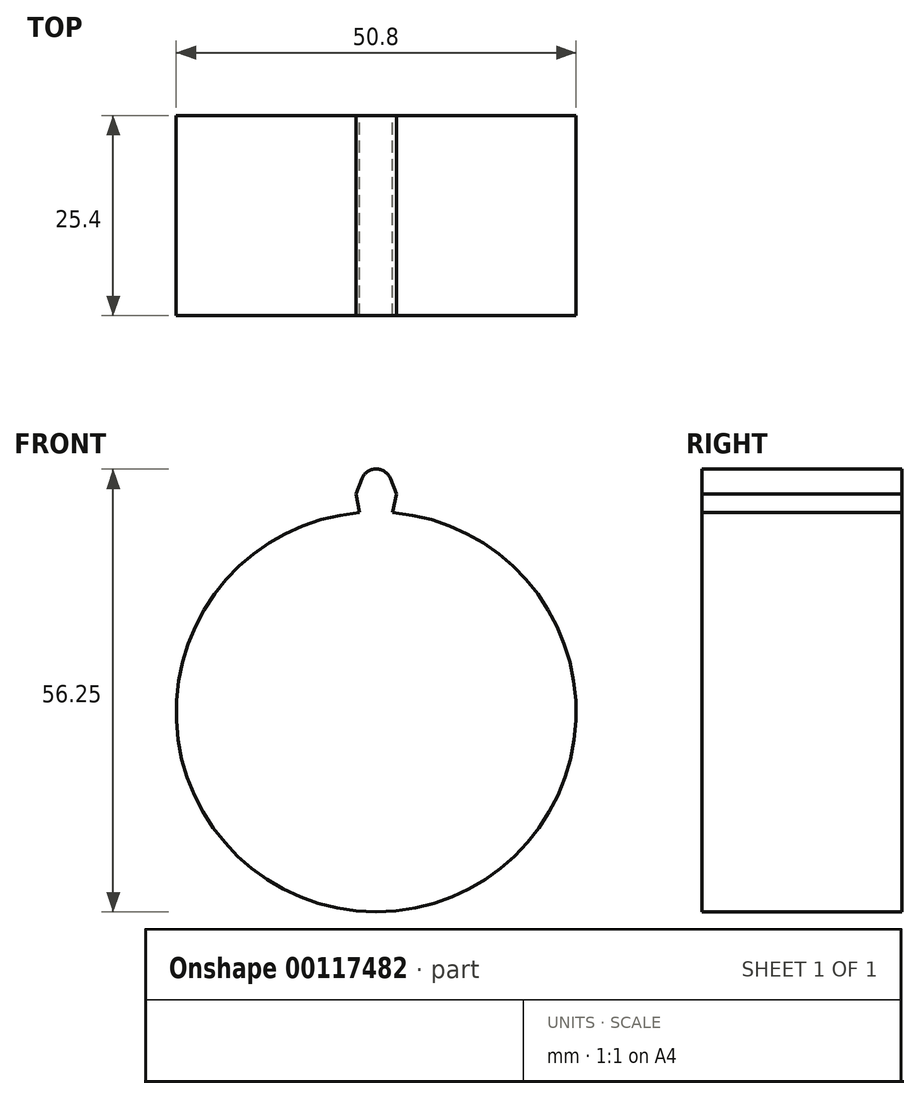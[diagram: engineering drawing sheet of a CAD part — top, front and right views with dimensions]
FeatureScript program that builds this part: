
annotation { "Feature Type Name" : "Feature", "Feature Type Description" : "" }
export const myFeature = defineFeature(function(context is Context, id is Id, definition is map)
    precondition{}
    {
        {
            var Q0;
            Q0=qCreatedBy(makeId("Front.planeOp"),FACE);
            var sketch = newSketch(context, id + "F0", { "sketchPlane" : qUnion([Q0])});
            skCircle(sketch, "E0", {"center": v(0, 0) * mm, "radius": 25.4 * mm});
            skSolve(sketch);
        }
        {
            var Q0;
            Q0=makeQuery(id+"F0.imprint","IMPRINT",FACE,{"disambiguationData":[TD([[makeQuery(id+"F0.imprint","IMPRINT",EDGE,{"derivedFrom":sQuery(id+"F0.wireOp",EDGE,"E0")}),1.0]])]});
            extrude(context, id + "F1", {"entities" : qUnion([Q0]), "depth" : 25.4 * mm});
        }
        {
            var Q0;
            Q0=qCreatedBy(makeId("Right.planeOp"),FACE);
            var sketch = newSketch(context, id + "F2", { "sketchPlane" : qUnion([Q0])});
            skLineSegment(sketch, "E1", {"start": v(0, 0) * mm, "end": v(-37.08, 0) * mm, "construction": true});
            skSolve(sketch);
        }
        {
            var Q0;
            Q0=qCreatedBy(makeId("Front.planeOp"),FACE);
            var sketch = newSketch(context, id + "F3", { "sketchPlane" : qUnion([Q0])});
            skLineSegment(sketch, "E2", {"start": v(2.04, 25.01) * mm, "end": v(2.58, 27.67) * mm});
            skLineSegment(sketch, "E3.MirrorCS", {"start": v(-2.04, 25.01) * mm, "end": v(-2.58, 27.67) * mm});
            skLineSegment(sketch, "E4", {"start": v(2.58, 27.67) * mm, "end": v(1.8, 29.63) * mm});
            skLineSegment(sketch, "E5.MirrorCS", {"start": v(-2.58, 27.67) * mm, "end": v(-1.8, 29.63) * mm});
            skArc(sketch, "E6", {"start": v(-1.8, 29.63) * mm, "mid": v(0, 30.85) * mm, "end": v(1.8, 29.63) * mm});
            skArc(sketch, "E7", {"start": v(2.04, 25.01) * mm, "mid": v(0, 25.1) * mm, "end": v(-2.04, 25.01) * mm});
            skSolve(sketch);
        }
        {
            var Q0;
            Q0=makeQuery(id+"F3.imprint","IMPRINT",FACE,{"disambiguationData":[TD([[makeQuery(id+"F3.imprint","IMPRINT",EDGE,{"derivedFrom":sQuery(id+"F3.wireOp",EDGE,"E2")}),1.0]])]});
            extrude(context, id + "F4", {"entities" : qUnion([Q0]), "operationType" : NewBodyOperationType.ADD, "depth" : 25.4 * mm});
        }
    });
